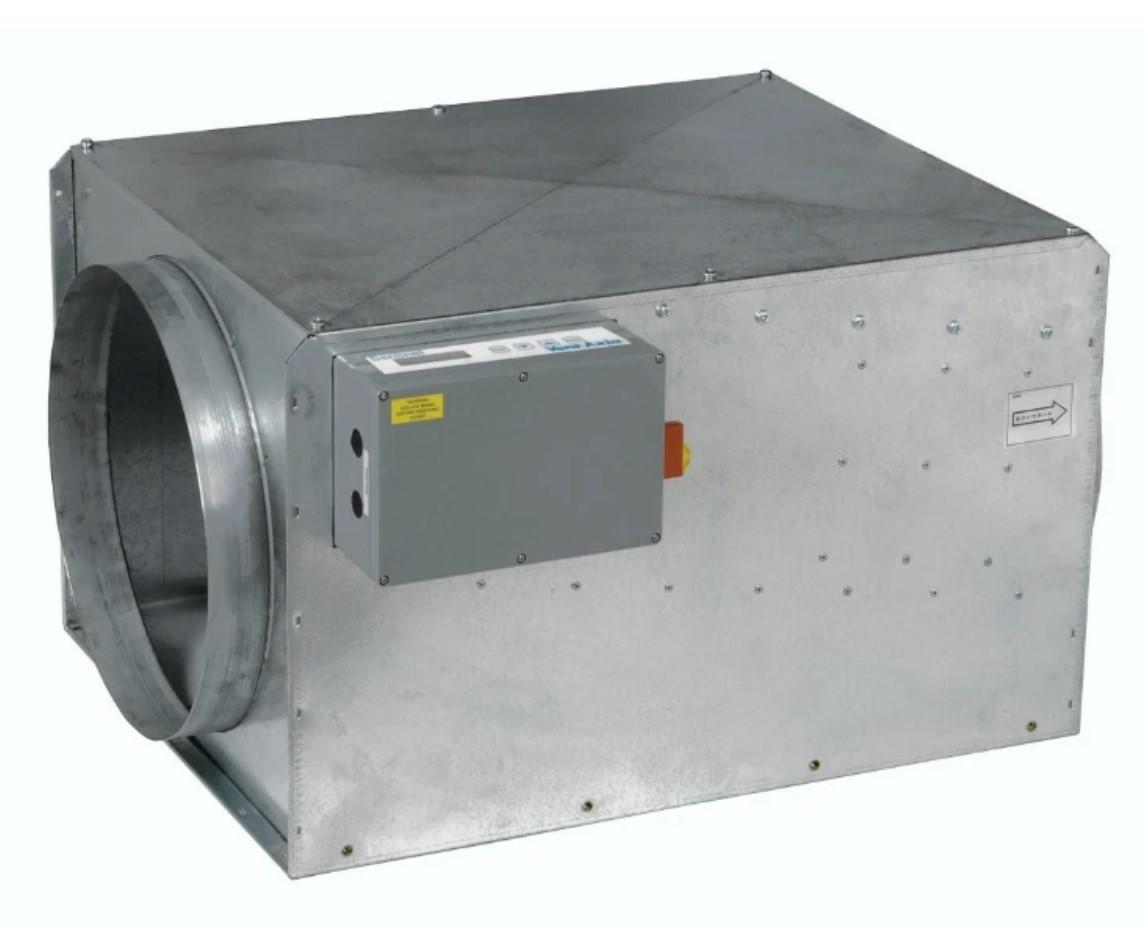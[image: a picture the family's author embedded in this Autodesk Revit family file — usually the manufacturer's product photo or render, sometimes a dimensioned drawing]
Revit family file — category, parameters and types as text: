
# Revit family: CADS_Vent-Axia_MechEquip_Fan_SENT_DBoxTwin - SUPPLY
name_source: partatom
category: Mechanical Equipment
units: mm (PartAtom-declared; Revit-internal decimal feet)

## family parameters
Classification = None
Cut with Voids When Loaded = No
Host = Face
OmniClass Number = 23.75.35.17.11
OmniClass Title = Fans for Air Ductwork
Part Type = Normal
Room Calculation Point = No
Round Connector Dimension = Use Diameter
Shared = No

## types (13) — shared parameters
AirflowRateRange = 0.0 L/s
AssemblyPlace = UNKNOWN
AssetType = FIXED
Default Elevation = 1219 mm
DurationUnit = Year
EBHoffset = 206 mm
EBVoffset = 80 mm
ExteriorInsulation = No
Fitting Type = Ignore
GrossWeight = 0.00 kg
HasProtectiveEarth = No
IsExtendedWarranty = No
ManufacturerAddress = Fleming Way
Crawley 
RH10 9YX
Quantity = 1
RatedCurrent = 0 A
RatedVoltage = 0 V
SpigotCLHeight = 62 mm
Status = New
Type Image = <None>
WarrantyGuarantor = Vent-Axia Limited
WorkingPressure = 0.0 Pa
zero-valued in all types: CADS_Index, CADS_Usage, ExpectedServiceLife, H, NumberOfPoles, OutOffset, W

## per-type parameters (varying)
| type | L | ModelReference | NominalDiameter | NominalHeight | NominalLength | NominalWidth |
| SENT100T | 610 mm  [stored 2.00131 ft] | SENTINEL 100T HEIRARCHY | 100 mm  [stored 0.328084 ft] | 256 mm  [stored 0.839895 ft] | 610 mm  [stored 2.00131 ft] | 591 mm  [stored 1.93898 ft] |
| SENT125T | 610 mm  [stored 2.00131 ft] | SENTINEL 125T HEIRARCHY | 125 mm  [stored 0.410105 ft] | 256 mm  [stored 0.839895 ft] | 610 mm  [stored 2.00131 ft] | 591 mm  [stored 1.93898 ft] |
| SENT125T/CP | 610 mm  [stored 2.00131 ft] | SENTINEL 125 TWIN CP | 125 mm  [stored 0.410105 ft] | 256 mm  [stored 0.839895 ft] | 610 mm  [stored 2.00131 ft] | 591 mm  [stored 1.93898 ft] |
| SENT150T | 610 mm  [stored 2.00131 ft] | SENTINEL 150 TWIN | 150 mm | 256 mm  [stored 0.839895 ft] | 610 mm  [stored 2.00131 ft] | 591 mm  [stored 1.93898 ft] |
| SENT200T | 801 mm | SENTINEL 200T HIERARCHY | 200 mm  [stored 0.656168 ft] | 343 mm | 801 mm | 703 mm |
| SENT250S/CP | 925 mm | SENTINEL 250 CONST.PRESS | 250 mm  [stored 0.82021 ft] | 354 mm | 925 mm | 798 mm |
| SENT250T | 925 mm | SENTINEL 250T HIERARCHY | 250 mm  [stored 0.82021 ft] | 354 mm | 925 mm | 798 mm |
| SENT250T/CP | 925 mm | SENTINEL 250 TWIN CP | 315 mm | 354 mm | 925 mm | 798 mm |
| SENT315T | 1255 mm | SENTINEL 315T HIERARCHY | 315 mm | 536 mm | 1255 mm | 1145 mm |
| SENT315T/CP | 1255 mm | SENTINEL 315 TWIN CP | 315 mm | 536 mm | 1255 mm | 1145 mm |
| SENT400T | 1255 mm | SENTINEL 400T HIERARCHY | 400 mm | 536 mm | 1255 mm | 1145 mm |
| SENT400T/CP | 1255 mm | SENTINEL 400 TWIN CP | 400 mm | 536 mm | 1255 mm | 1145 mm |
| SENT500T | 1492 mm | SENTINEL 500T HIERARCHY | 500 mm | 675 mm | 1492 mm | 1533 mm |

note: column(s) folded — value = type name in every type: ModelNumber

note: [stored X ft] marks values corroborated as IEEE doubles in the binary element streams (Revit-internal decimal feet)

## geometry (parser evidence)
native form markers: Sweep x3
no freeform markers — native parametric forms only
